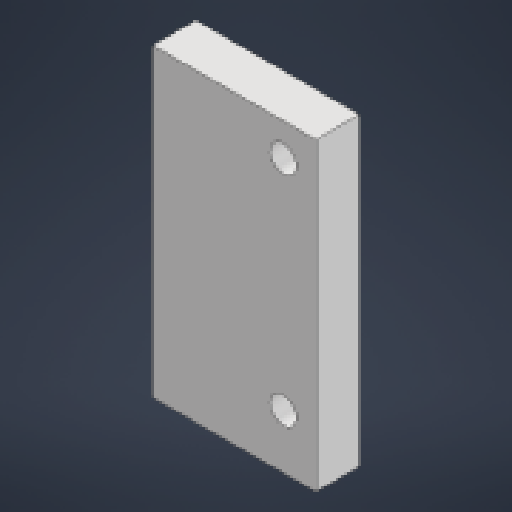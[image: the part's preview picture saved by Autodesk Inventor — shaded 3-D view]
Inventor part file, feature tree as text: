
AUTODESK INVENTOR PART (.ipt)
format: ipt  version: 2025 (Build 290162000, 162)  size: 195,584 bytes
history: native  units: mm
features: extrude x4, sketch x4, fillet x2, reference x2, other x2
ambient origin geometry x8: Origin, YZ Plane, XZ Plane, XY Plane, X Axis, Y Axis, Z Axis, Center Point
bodies: 实体1 (feature_tree)
feature tree (14):
  extrude  "拉伸1"  Depth=4.0mm
  extrude  "拉伸2"  Depth=25.0mm TaperAngle=0.0deg
  extrude  "拉伸3"  Depth=25.0mm TaperAngle=0.0deg
  fillet  "圆角1"  Radius=6.0mm
  extrude  "拉伸4"  Depth=4.0mm TaperAngle=0.0deg
  fillet  "圆角2"  Radius=4.0mm
  sketch  "草图1"  dims[d1=4.0mm d2=0.0mm d3=15.0mm]
  reference  "参考1"
  sketch  "草图2"  dims[d4=28.0mm d5=25.0mm d6=0.0mm]
  reference  "参考2"
  sketch  "草图3"  dims[d7=20.0mm d8=25.0mm d9=0.0mm d10=6.0mm]
  sketch  "草图4"  dims[d11=6.0mm d12=25.0mm d13=0.0mm d14=4.0mm]
  other  "南京理工大学AllianceV3全向轮组装配(1).iam"
  other  "南京理工大学Alliance转接件-4孔_41"
